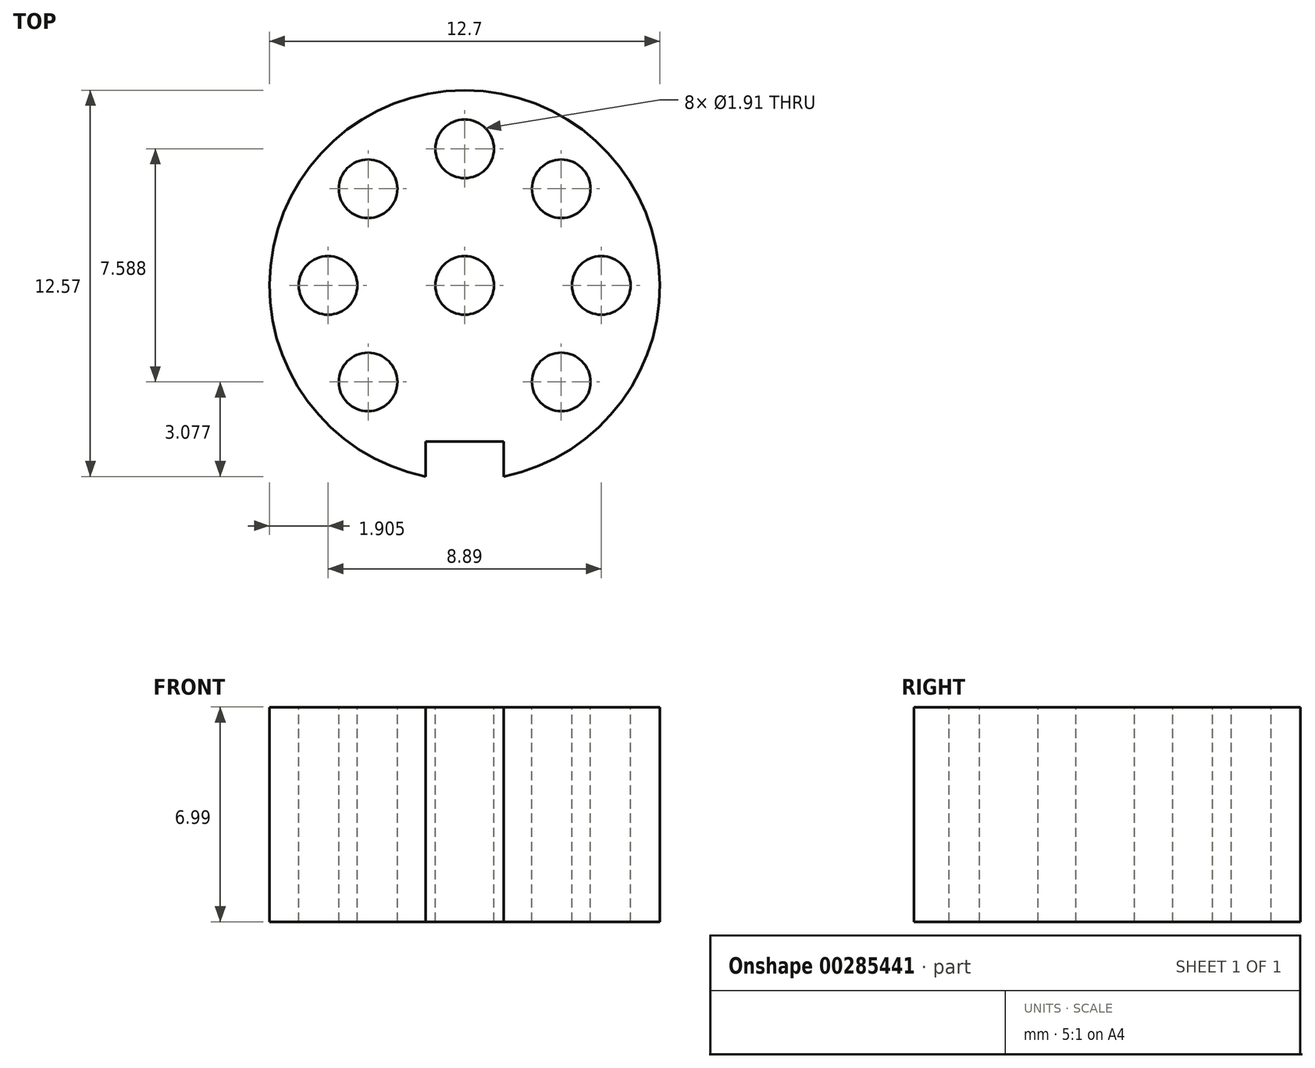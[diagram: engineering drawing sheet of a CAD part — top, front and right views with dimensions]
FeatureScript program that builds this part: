
annotation { "Feature Type Name" : "Feature", "Feature Type Description" : "" }
export const myFeature = defineFeature(function(context is Context, id is Id, definition is map)
    precondition{}
    {
        {
            var Q0;
            Q0=qCreatedBy(makeId("Top.planeOp"),FACE);
            var sketch = newSketch(context, id + "F0", { "sketchPlane" : qUnion([Q0])});
            skCircle(sketch, "E0", {"center": v(0, 0) * mm, "radius": 6.35 * mm});
            skSolve(sketch);
        }
        {
            var Q0;
            Q0 = qSketchRegion(id + "F0", true);
            extrude(context, id + "F1", {"entities" : qUnion([Q0]), "depth" : 7 * mm});
        }
        {
            var Q0;
            Q0=makeQuery(id+"F1.opExtrude","CAP_FACE",FACE,{"disambiguationData":[OSD([sQuery(id+"F0.wireOp",EDGE,"E0")])],"isStart":false});
            var sketch = newSketch(context, id + "F2", { "sketchPlane" : qUnion([Q0])});
            skCircle(sketch, "E1", {"center": v(0, 4.45) * mm, "radius": 0.95 * mm});
            skCircle(sketch, "E2", {"center": v(3.14, 3.14) * mm, "radius": 0.95 * mm});
            skCircle(sketch, "E3", {"center": v(3.14, -3.14) * mm, "radius": 0.95 * mm});
            skCircle(sketch, "E4", {"center": v(-3.14, 3.14) * mm, "radius": 0.95 * mm});
            skCircle(sketch, "E5", {"center": v(-3.14, -3.14) * mm, "radius": 0.95 * mm});
            skCircle(sketch, "E6", {"center": v(-4.45, 0) * mm, "radius": 0.95 * mm});
            skCircle(sketch, "E7", {"center": v(4.45, 0) * mm, "radius": 0.95 * mm});
            skCircle(sketch, "E8", {"center": v(0, 0) * mm, "radius": 0.95 * mm});
            skCircle(sketch, "E9", {"center": v(0, 0) * mm, "radius": 4.45 * mm, "construction": true});
            skLineSegment(sketch, "E10", {"start": v(0, 0) * mm, "end": v(-3.14, -3.14) * mm, "construction": true});
            skLineSegment(sketch, "E11", {"start": v(0, 0) * mm, "end": v(-3.14, 3.14) * mm, "construction": true});
            skLineSegment(sketch, "E12", {"start": v(0, 0) * mm, "end": v(3.14, 3.14) * mm, "construction": true});
            skLineSegment(sketch, "E13", {"start": v(0, 0) * mm, "end": v(3.14, -3.14) * mm, "construction": true});
            skLineSegment(sketch, "E14", {"start": v(0, 0) * mm, "end": v(-4.45, 0) * mm, "construction": true});
            skLineSegment(sketch, "E15", {"start": v(0, 0) * mm, "end": v(4.45, 0) * mm, "construction": true});
            skLineSegment(sketch, "E16", {"start": v(0, 0) * mm, "end": v(0, 4.45) * mm, "construction": true});
            skSolve(sketch);
        }
        {
            var Q0;
            Q0 = qSketchRegion(id + "F2", true);
            extrude(context, id + "F3", {"entities" : qUnion([Q0]), "operationType" : NewBodyOperationType.REMOVE, "endBound" : BoundingType.THROUGH_ALL, "oppositeDirection" : true, "depth" : 25.4 * mm});
        }
        {
            var Q0;
            Q0=makeQuery(id+"F1.opExtrude","CAP_FACE",FACE,{"disambiguationData":[OSD([sQuery(id+"F0.wireOp",EDGE,"E0")])],"isStart":false});
            var sketch = newSketch(context, id + "F4", { "sketchPlane" : qUnion([Q0])});
            skLineSegment(sketch, "E17", {"start": v(0, 0) * mm, "end": v(0, -5.08) * mm, "construction": true});
            skArc(sketch, "E18.0", {"start": v(-1.27, -6.22) * mm, "mid": v(0, -6.35) * mm, "end": v(1.27, -6.22) * mm});
            skLineSegment(sketch, "E19.top", {"start": v(1.27, -5.08) * mm, "end": v(-1.27, -5.08) * mm});
            skLineSegment(sketch, "E19.left", {"start": v(1.27, -6.22) * mm, "end": v(1.27, -5.08) * mm});
            skLineSegment(sketch, "E19.right", {"start": v(-1.27, -6.22) * mm, "end": v(-1.27, -5.08) * mm});
            skSolve(sketch);
        }
        {
            var Q0;
            Q0 = qSketchRegion(id + "F4", true);
            extrude(context, id + "F5", {"entities" : qUnion([Q0]), "operationType" : NewBodyOperationType.REMOVE, "endBound" : BoundingType.THROUGH_ALL, "oppositeDirection" : true, "depth" : 25.4 * mm});
        }
    });
